# Revit family: Arcos_LED-W
name_source: partatom
category: Lighting Fixtures
revit_build: Autodesk Revit 2014 (Build: 20130308_1515(x64)
units: mm (PartAtom-declared; Revit-internal decimal feet)

## types (5) — shared parameters
Apparent Load = 4 VA
Assembly Code = D5020200
Color Filter = 16777215
Description = Wall Arcos 54L is an ADA-compliant extruded aluminum LED luminaire in the popular Arcos curved shape
Dimming Lamp Color Temperature Shift = <None>
Emit Shape Visible in Rendering = No
Emit from Rectangle Width = 2"
Fixture distribution = Asymmetric Indirect
Lamp = LED
Load Classification = Lighting
Manufacturer = LiteControl
Model = Arcos LED Wall
Mounting = Wall-Mounted
Photometric Web File = generic
Power Factor = 1
Product Documentation Link = https://hubbellcdn.com
Product Material = Paint - Hubbell - Matte White
Product Page URL = https://www.hubbell.com
Reflector Finish = Glass - Hubbell - White
Tilt Angle = -90.00°
Type Comments = Lighting Fixtures
URL = https://www.hubbell.com
Warranty = 5 years Warranty
Watts = 4 W

## per-type parameters (varying)
| type | Emit from Rectangle Length | zz Length 1 |
| Arcos-W-06 | 70" | 72" |
| Arcos-W-02 | 22" | 24" |
| Arcos-W-03 | 34" | 36" |
| Arcos-W-04 | 46" | 48" |
| Arcos-W-08 | 94" | 96" |

## geometry (parser evidence)
native form markers: Blend x10, Sweep x1
no freeform markers — native parametric forms only
